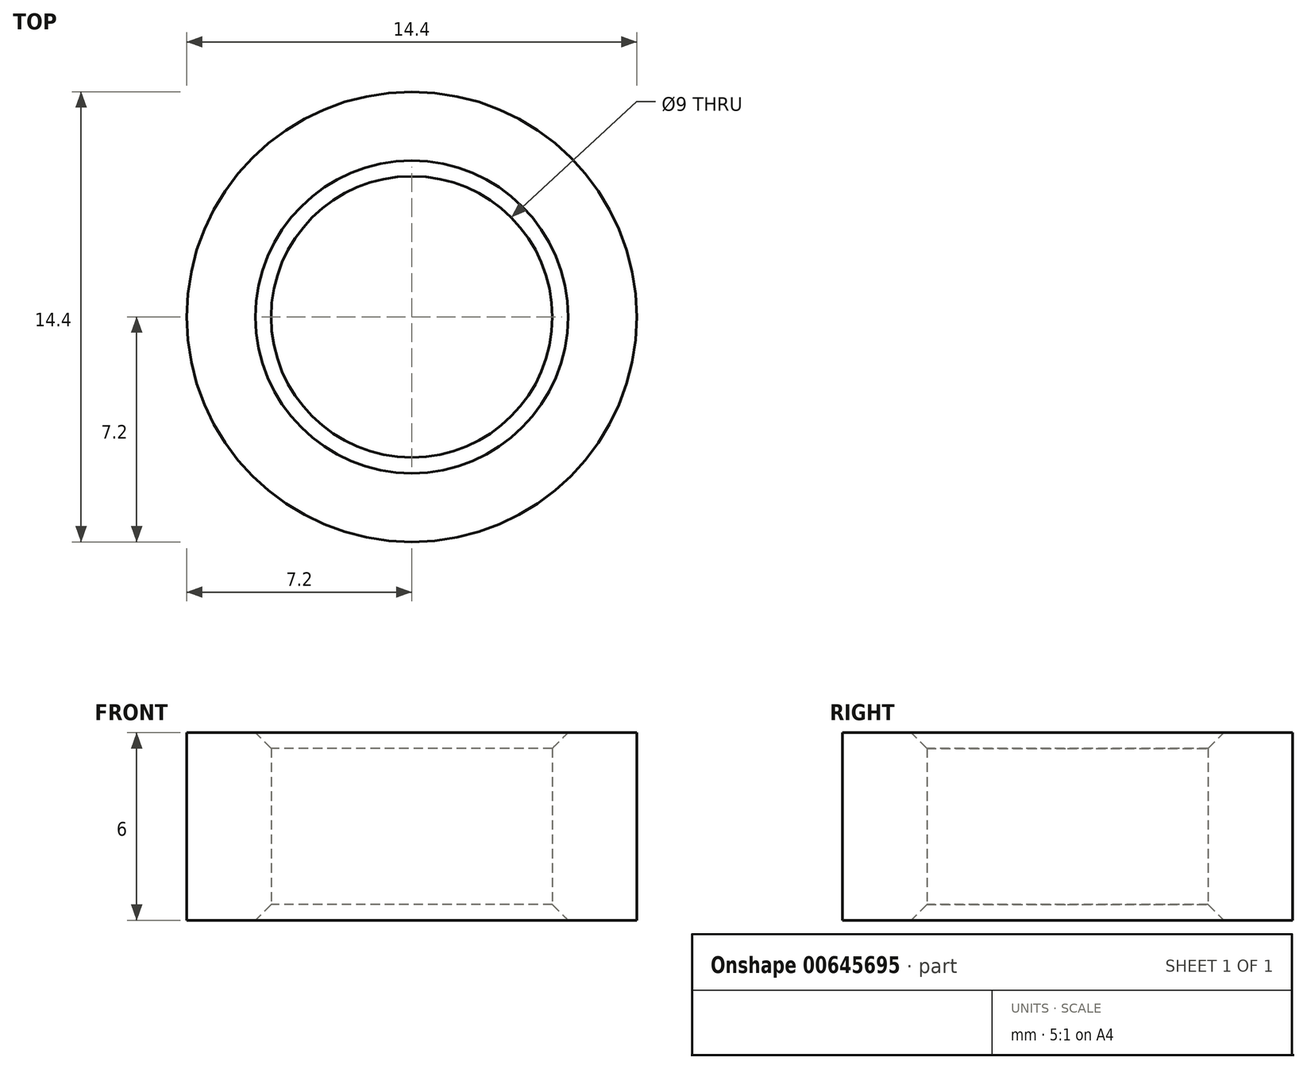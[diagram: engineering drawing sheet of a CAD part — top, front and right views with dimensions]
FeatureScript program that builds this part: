
annotation { "Feature Type Name" : "Feature", "Feature Type Description" : "" }
export const myFeature = defineFeature(function(context is Context, id is Id, definition is map)
    precondition{}
    {
        {
            var Q0;
            Q0=qCreatedBy(makeId("Top.planeOp"),FACE);
            var sketch = newSketch(context, id + "F0", { "sketchPlane" : qUnion([Q0])});
            skCircle(sketch, "E0", {"center": v(0, 0) * mm, "radius": 7.2 * mm});
            skCircle(sketch, "E1", {"center": v(0, 0) * mm, "radius": 4.5 * mm});
            skSolve(sketch);
        }
        {
            var Q0;
            Q0=qSketchRegion(id+"F0",true);
            extrude(context, id + "F1", {"entities" : qUnion([Q0]), "depth" : 6 * mm, "offsetDistance" : 25.4 * mm});
        }
        {
            var Q0;
            Q0=makeQuery(id+"F1.opExtrude","CAP_EDGE",EDGE,{"disambiguationData":[OSD([sQuery(id+"F0.wireOp",EDGE,"E1")])],"isStart":true});
            var Q1;
            Q1=makeQuery(id+"F1.opExtrude","SWEPT_FACE",FACE,{"disambiguationData":[OSD([sQuery(id+"F0.wireOp",EDGE,"E1")])]});
            chamfer(context, id + "F2", {"entities" : qUnion([Q0, Q1]), "chamferType" : ChamferType.OFFSET_ANGLE, "width" : 0.5 * mm, "oppositeDirection" : false, "angle" : 45 * degree, "tangentPropagation" : true});
        }
    });
